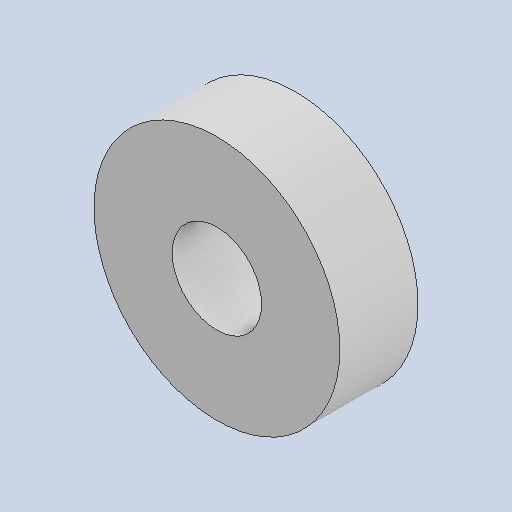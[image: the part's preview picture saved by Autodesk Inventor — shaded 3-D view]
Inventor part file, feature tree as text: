
AUTODESK INVENTOR PART (.ipt)
format: ipt  version: 2022 (Build 260153000, 153)  size: 92,672 bytes
history: native  units: in
note: dims shown in document units (in); Inventor stores cm internally (conversion verified against a paired STEP export)
features: other x3, sketch x1
ambient origin geometry x8: Origin, YZ Plane, XZ Plane, XY Plane, X Axis, Y Axis, Z Axis, Center Point
bodies: Solid1 (feature_tree)
feature tree (4):
  other  "608.ipt"
  other  "Solid1::608.ipt"
  other  "TaggingFeature1"
  sketch  "Sketch1"  dims[d0=0.3937in]
